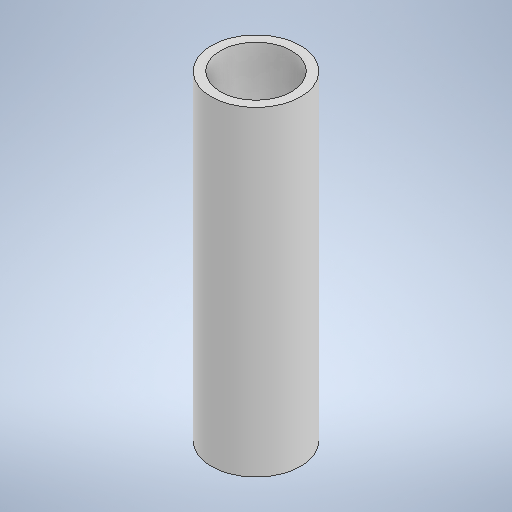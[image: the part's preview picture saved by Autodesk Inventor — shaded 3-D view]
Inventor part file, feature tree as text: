
AUTODESK INVENTOR PART (.ipt)
format: ipt  version: 2025.1 (Build 291241000, 241)  size: 230,912 bytes
history: native  units: mm
features: extrude x1, sketch x1
ambient origin geometry x8: Origin, YZ Plane, XZ Plane, XY Plane, X Axis, Y Axis, Z Axis, Center Point
bodies: Solid1 (feature_tree)
feature tree (2):
  extrude  "Extrusion1"  Depth=18.0mm
  sketch  "Sketch1"  dims[d0=5.0mm d1=4.0mm d2=18.0mm d3=0.0mm]
